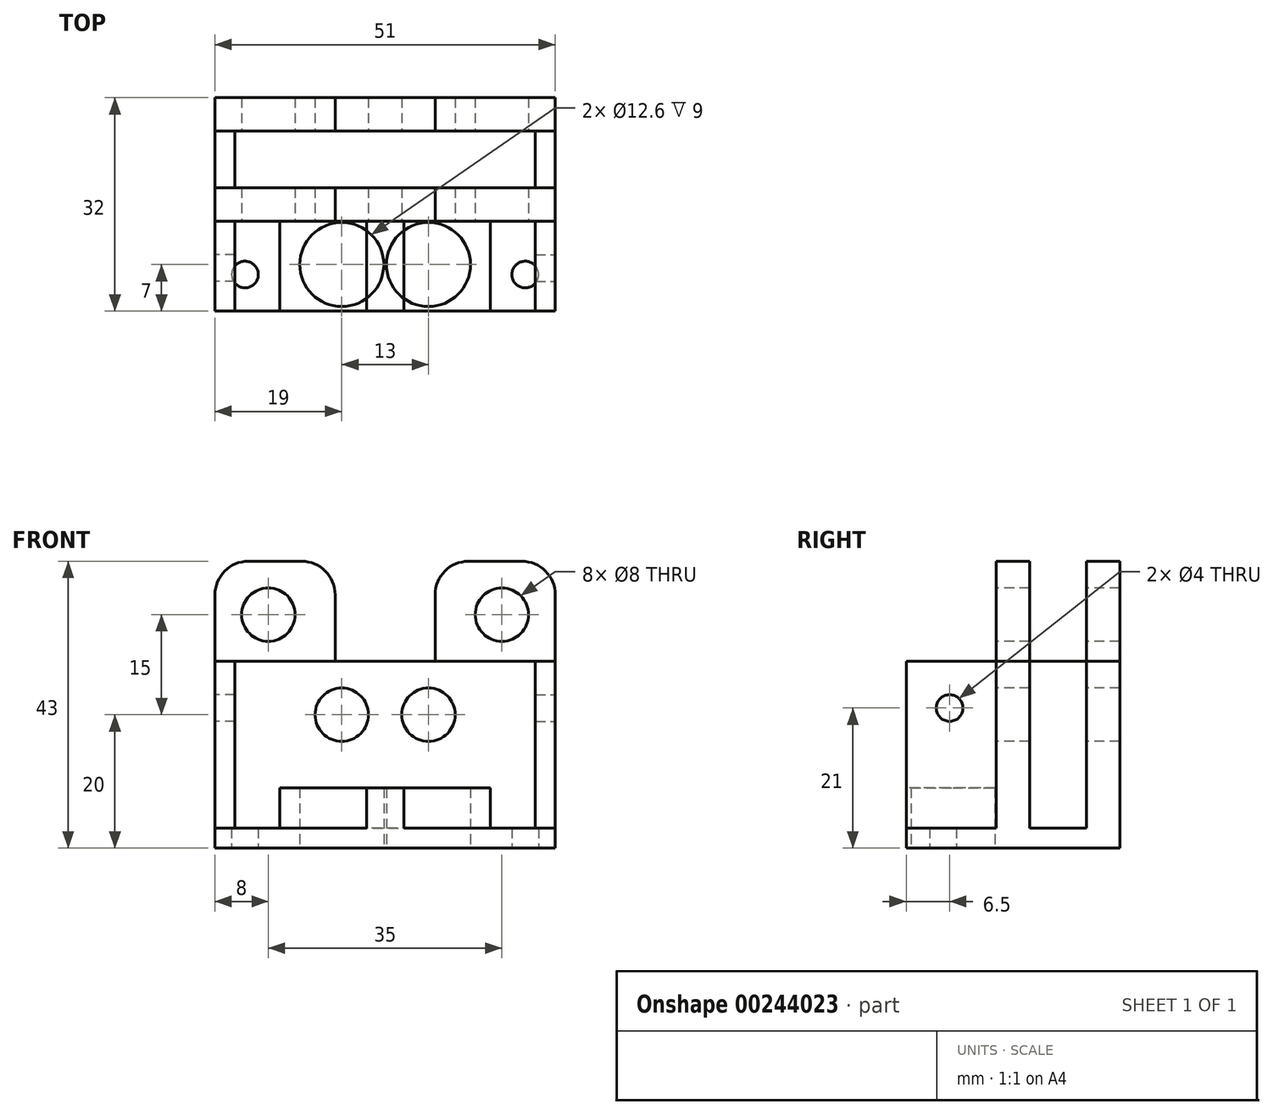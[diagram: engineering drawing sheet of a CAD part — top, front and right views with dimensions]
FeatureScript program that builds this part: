
annotation { "Feature Type Name" : "Feature", "Feature Type Description" : "" }
export const myFeature = defineFeature(function(context is Context, id is Id, definition is map)
    precondition{}
    {
        {
            var Q0;
            Q0=qCreatedBy(makeId("Top.planeOp"),FACE);
            var sketch = newSketch(context, id + "F0", { "sketchPlane" : qUnion([Q0])});
            skLineSegment(sketch, "E0.bottom", {"start": v(-25.5, 16) * mm, "end": v(25.5, 16) * mm});
            skLineSegment(sketch, "E0.top", {"start": v(-25.5, -16) * mm, "end": v(25.5, -16) * mm});
            skLineSegment(sketch, "E0.left", {"start": v(-25.5, 16) * mm, "end": v(-25.5, -16) * mm});
            skLineSegment(sketch, "E0.right", {"start": v(25.5, 16) * mm, "end": v(25.5, -16) * mm});
            skPoint(sketch, "E0.middle", {"position": v(0, 0) * mm});
            skCircle(sketch, "E1", {"center": v(21, -10.5) * mm, "radius": 2 * mm});
            skSolve(sketch);
        }
        {
            var Q0;
            Q0=makeQuery(id+"F0.imprint","IMPRINT",FACE,{"disambiguationData":[TD([[makeQuery(id+"F0.imprint","IMPRINT",EDGE,{"derivedFrom":sQuery(id+"F0.wireOp",EDGE,"E0.bottom")}),-1.0]])]});
            extrude(context, id + "F1", {"entities" : qUnion([Q0]), "depth" : 3 * mm});
        }
        {
            var Q0;
            Q0=makeQuery(id+"F1.opExtrude","CAP_FACE",FACE,{"disambiguationData":[OSD([sQuery(id+"F0.wireOp",EDGE,"E0.bottom"),sQuery(id+"F0.wireOp",EDGE,"E0.top"),sQuery(id+"F0.wireOp",EDGE,"E0.left"),sQuery(id+"F0.wireOp",EDGE,"E0.right"),sQuery(id+"F0.wireOp",EDGE,"E1")])],"isStart":false});
            var sketch = newSketch(context, id + "F2", { "sketchPlane" : qUnion([Q0])});
            skLineSegment(sketch, "E2", {"start": v(-22.5, 11) * mm, "end": v(25.5, 11) * mm});
            skLineSegment(sketch, "E3", {"start": v(-22.5, 2.5) * mm, "end": v(25.5, 2.5) * mm});
            skLineSegment(sketch, "E4.trimOffspring", {"start": v(-22.5, 2.5) * mm, "end": v(-22.5, 11) * mm});
            skLineSegment(sketch, "E5", {"start": v(-15.8, -2.5) * mm, "end": v(-15.8, -16) * mm});
            skLineSegment(sketch, "E6", {"start": v(2.8, -16) * mm, "end": v(2.8, -2.5) * mm});
            skLineSegment(sketch, "E7", {"start": v(-22.5, -2.5) * mm, "end": v(-22.5, -16) * mm});
            skLineSegment(sketch, "E8", {"start": v(-22.5, -2.5) * mm, "end": v(25.5, -2.5) * mm});
            skCircle(sketch, "E9", {"center": v(-6.5, -9) * mm, "radius": 6.3 * mm});
            skSolve(sketch);
        }
        {
            var Q0;
            {var subQ10=sQuery(id+"F2.wireOp",EDGE,"E2");Q0=makeQuery(id+"F2.imprint","IMPRINT",FACE,{"disambiguationData":[TD([[makeQuery(id+"F2.imprint","IMPRINT",EDGE,{"derivedFrom":subQ10}),1.0]])]});}
            extrude(context, id + "F3", {"entities" : qUnion([Q0]), "operationType" : NewBodyOperationType.ADD, "depth" : 25 * mm});
        }
        {
            var Q0;
            {var subQ1=sQuery(id+"F2.wireOp",EDGE,"E5");Q0=makeQuery(id+"F2.imprint","IMPRINT",FACE,{"disambiguationData":[TD([[makeQuery(id+"F2.imprint","IMPRINT",EDGE,{"derivedFrom":subQ1}),1.0]])]});}
            extrude(context, id + "F4", {"entities" : qUnion([Q0]), "operationType" : NewBodyOperationType.ADD, "depth" : 6 * mm});
        }
        {
            var Q0;
            {var subQ0=sQuery(id+"F0.wireOp",EDGE,"E1");var subQ1=sQuery(id+"F0.wireOp",EDGE,"E0.right");var subQ4=sQuery(id+"F0.wireOp",EDGE,"E0.top");var subQ5=sQuery(id+"F0.wireOp",EDGE,"E0.bottom");Q0=makeQuery(id+"F4.boolean.opBoolean","SPLIT",FACE,{"disambiguationData":[TD([makeQuery(id+"F4.opExtrude","SWEPT_FACE",FACE,{"disambiguationData":[OSD([sQuery(id+"F2.wireOp",EDGE,"E9")])]})])],"derivedFrom":makeQuery(id+"F3.boolean.opBoolean","SPLIT",FACE,{"disambiguationData":[TD([makeQuery(id+"F1.opExtrude","SWEPT_FACE",FACE,{"disambiguationData":[OSD([subQ4])]})])],"derivedFrom":makeQuery(id+"F1.opExtrude","CAP_FACE",FACE,{"disambiguationData":[OSD([subQ5,subQ4,sQuery(id+"F0.wireOp",EDGE,"E0.left"),subQ1,subQ0])],"isStart":false})})});}
            extrude(context, id + "F5", {"entities" : qUnion([Q0]), "operationType" : NewBodyOperationType.REMOVE, "endBound" : BoundingType.UP_TO_NEXT, "oppositeDirection" : true, "depth" : 25 * mm});
        }
        {
            var Q0;
            Q0=makeQuery(id+"F3.opExtrude","CAP_FACE",FACE,{"disambiguationData":[OSD([sQuery(id+"F0.wireOp",EDGE,"E0.bottom"),sQuery(id+"F0.wireOp",EDGE,"E0.top"),sQuery(id+"F0.wireOp",EDGE,"E0.left"),sQuery(id+"F0.wireOp",EDGE,"E0.right"),sQuery(id+"F2.wireOp",EDGE,"E2"),sQuery(id+"F2.wireOp",EDGE,"E3"),sQuery(id+"F2.wireOp",EDGE,"E4.trimOffspring"),sQuery(id+"F2.wireOp",EDGE,"E7"),sQuery(id+"F2.wireOp",EDGE,"E8")])],"isStart":false});
            var sketch = newSketch(context, id + "F6", { "sketchPlane" : qUnion([Q0])});
            skLineSegment(sketch, "E10", {"start": v(7.5, -2.5) * mm, "end": v(7.5, 2.5) * mm});
            skLineSegment(sketch, "E11", {"start": v(7.5, 11) * mm, "end": v(7.5, 16) * mm});
            skSolve(sketch);
        }
        {
            var Q0;
            Q0 = qSketchRegion(id + "F6", true);
            var Q1;
            {var subQ0=sQuery(id+"F6.wireOp",EDGE,"E11");Q1=makeQuery(id+"F6.imprint","IMPRINT",FACE,{"disambiguationData":[TD([[makeQuery(id+"F6.imprint","IMPRINT",EDGE,{"derivedFrom":subQ0}),-1.0]])]});}
            var Q2;
            {var subQ0=sQuery(id+"F6.wireOp",EDGE,"E10");Q2=makeQuery(id+"F6.imprint","IMPRINT",FACE,{"disambiguationData":[TD([[makeQuery(id+"F6.imprint","IMPRINT",EDGE,{"derivedFrom":subQ0}),-1.0]])]});}
            extrude(context, id + "F7", {"entities" : qUnion([Q0, Q1, Q2]), "operationType" : NewBodyOperationType.ADD, "depth" : 15 * mm});
        }
        {
            var Q0;
            Q0=makeQuery(id+"F3.opExtrude","SWEPT_FACE",FACE,{"disambiguationData":[OSD([sQuery(id+"F2.wireOp",EDGE,"E8")])]});
            var sketch = newSketch(context, id + "F8", { "sketchPlane" : qUnion([Q0])});
            skCircle(sketch, "E12", {"center": v(-6.5, 20) * mm, "radius": 4 * mm});
            skCircle(sketch, "E13", {"center": v(17.5, 35) * mm, "radius": 4 * mm});
            skSolve(sketch);
        }
        {
            var Q0;
            Q0=makeQuery(id+"F8.imprint","IMPRINT",FACE,{"disambiguationData":[TD([[makeQuery(id+"F8.imprint","IMPRINT",EDGE,{"derivedFrom":sQuery(id+"F8.wireOp",EDGE,"E12")}),1.0]])]});
            extrude(context, id + "F9", {"entities" : qUnion([Q0]), "operationType" : NewBodyOperationType.REMOVE, "endBound" : BoundingType.THROUGH_ALL, "oppositeDirection" : true, "depth" : 25 * mm});
        }
        {
            var Q0;
            Q0=makeQuery(id+"F8.imprint","IMPRINT",FACE,{"disambiguationData":[TD([[makeQuery(id+"F8.imprint","IMPRINT",EDGE,{"derivedFrom":sQuery(id+"F8.wireOp",EDGE,"E13")}),1.0]])]});
            extrude(context, id + "F10", {"entities" : qUnion([Q0]), "operationType" : NewBodyOperationType.REMOVE, "endBound" : BoundingType.THROUGH_ALL, "oppositeDirection" : true, "depth" : 25 * mm});
        }
        {
            var Q0;
            {var subQ0=sQuery(id+"F0.wireOp",EDGE,"E0.right");var subQ1=makeQuery(id+"F1.opExtrude","CAP_EDGE",EDGE,{"disambiguationData":[OSD([subQ0])],"isStart":false});Q0=makeQuery(id+"F7.opExtrude","CAP_EDGE",EDGE,{"disambiguationData":[OSD([subQ0]),TDD([makeQuery(id+"F6.imprint","IMPRINT",EDGE,{"derivedFrom":makeQuery(id+"F3.opExtrude","CAP_EDGE",EDGE,{"disambiguationData":[OSD([subQ0]),TDD([makeQuery(id+"F2.imprint","IMPRINT",EDGE,{"disambiguationData":[TD([[makeQuery(id+"F2.imprint","INTERSECT",VERTEX,{"derivedFrom":[subQ1,sQuery(id+"F2.wireOp",EDGE,"E3")]}),-1.0]])],"derivedFrom":subQ1})])],"isStart":false})})])],"isStart":false});}
            var Q1;
            {var subQ0=sQuery(id+"F0.wireOp",EDGE,"E0.right");var subQ1=makeQuery(id+"F1.opExtrude","CAP_EDGE",EDGE,{"disambiguationData":[OSD([subQ0])],"isStart":false});Q1=makeQuery(id+"F7.opExtrude","CAP_EDGE",EDGE,{"disambiguationData":[OSD([subQ0]),TDD([makeQuery(id+"F6.imprint","IMPRINT",EDGE,{"derivedFrom":makeQuery(id+"F3.opExtrude","CAP_EDGE",EDGE,{"disambiguationData":[OSD([subQ0]),TDD([makeQuery(id+"F2.imprint","IMPRINT",EDGE,{"disambiguationData":[TD([[makeQuery(id+"F2.imprint","INTERSECT",VERTEX,{"derivedFrom":[makeQuery(id+"F1.opExtrude","CAP_EDGE",EDGE,{"disambiguationData":[OSD([sQuery(id+"F0.wireOp",EDGE,"E0.bottom")])],"isStart":false}),subQ1]}),-1.0]])],"derivedFrom":subQ1})])],"isStart":false})})])],"isStart":false});}
            var Q2;
            Q2=makeQuery(id+"F7.opExtrude","CAP_EDGE",EDGE,{"disambiguationData":[OSD([sQuery(id+"F6.wireOp",EDGE,"E11")])],"isStart":false});
            var Q3;
            Q3=makeQuery(id+"F7.opExtrude","CAP_EDGE",EDGE,{"disambiguationData":[OSD([sQuery(id+"F6.wireOp",EDGE,"E10")])],"isStart":false});
            var Q4;
            Q4=makeQuery(id+"F7.opExtrude","CAP_EDGE",EDGE,{"disambiguationData":[OSD([sQuery(id+"F6.wireOp",EDGE,"E11")])],"isStart":true});
            var Q5;
            Q5=makeQuery(id+"F7.opExtrude","CAP_EDGE",EDGE,{"disambiguationData":[OSD([sQuery(id+"F6.wireOp",EDGE,"E10")])],"isStart":true});
            fillet(context, id + "F11", {"entities" : qUnion([Q0, Q1, Q2, Q3, Q4, Q5]), "radius" : 5 * mm, "tangentPropagation" : true, "allowEdgeOverflow" : false});
        }
        {
            var Q0;
            {var subQ0=sQuery(id+"F0.wireOp",EDGE,"E0.left");Q0=makeQuery(id+"F3.boolean.opBoolean","MERGE",FACE,{"derivedFrom":[makeQuery(id+"F1.opExtrude","SWEPT_FACE",FACE,{"disambiguationData":[OSD([subQ0])]}),makeQuery(id+"F3.opExtrude","SWEPT_FACE",FACE,{"disambiguationData":[OSD([subQ0])]})]});}
            var sketch = newSketch(context, id + "F12", { "sketchPlane" : qUnion([Q0])});
            skCircle(sketch, "E14", {"center": v(9.5, 21) * mm, "radius": 2 * mm});
            skSolve(sketch);
        }
        {
            var Q0;
            Q0=makeQuery(id+"F12.imprint","IMPRINT",FACE,{"disambiguationData":[TD([[makeQuery(id+"F12.imprint","IMPRINT",EDGE,{"derivedFrom":sQuery(id+"F12.wireOp",EDGE,"E14")}),1.0]])]});
            extrude(context, id + "F13", {"entities" : qUnion([Q0]), "operationType" : NewBodyOperationType.REMOVE, "endBound" : BoundingType.UP_TO_NEXT, "oppositeDirection" : true, "depth" : 25 * mm});
        }
        {
            var Q0;
            Q0=makeQuery(id+"F1.opExtrude","SWEPT_BODY",BODY,{"disambiguationData":[OSD([sQuery(id+"F0.wireOp",EDGE,"E0.bottom"),sQuery(id+"F0.wireOp",EDGE,"E0.top"),sQuery(id+"F0.wireOp",EDGE,"E0.left"),sQuery(id+"F0.wireOp",EDGE,"E0.right"),sQuery(id+"F0.wireOp",EDGE,"E1")])]});
            var Q1;
            Q1=qCreatedBy(makeId("Right.planeOp"),FACE);
            mirror(context, id + "F14", {"entities" : qUnion([Q0]), "mirrorPlane" : qUnion([Q1])});
        }
    });
